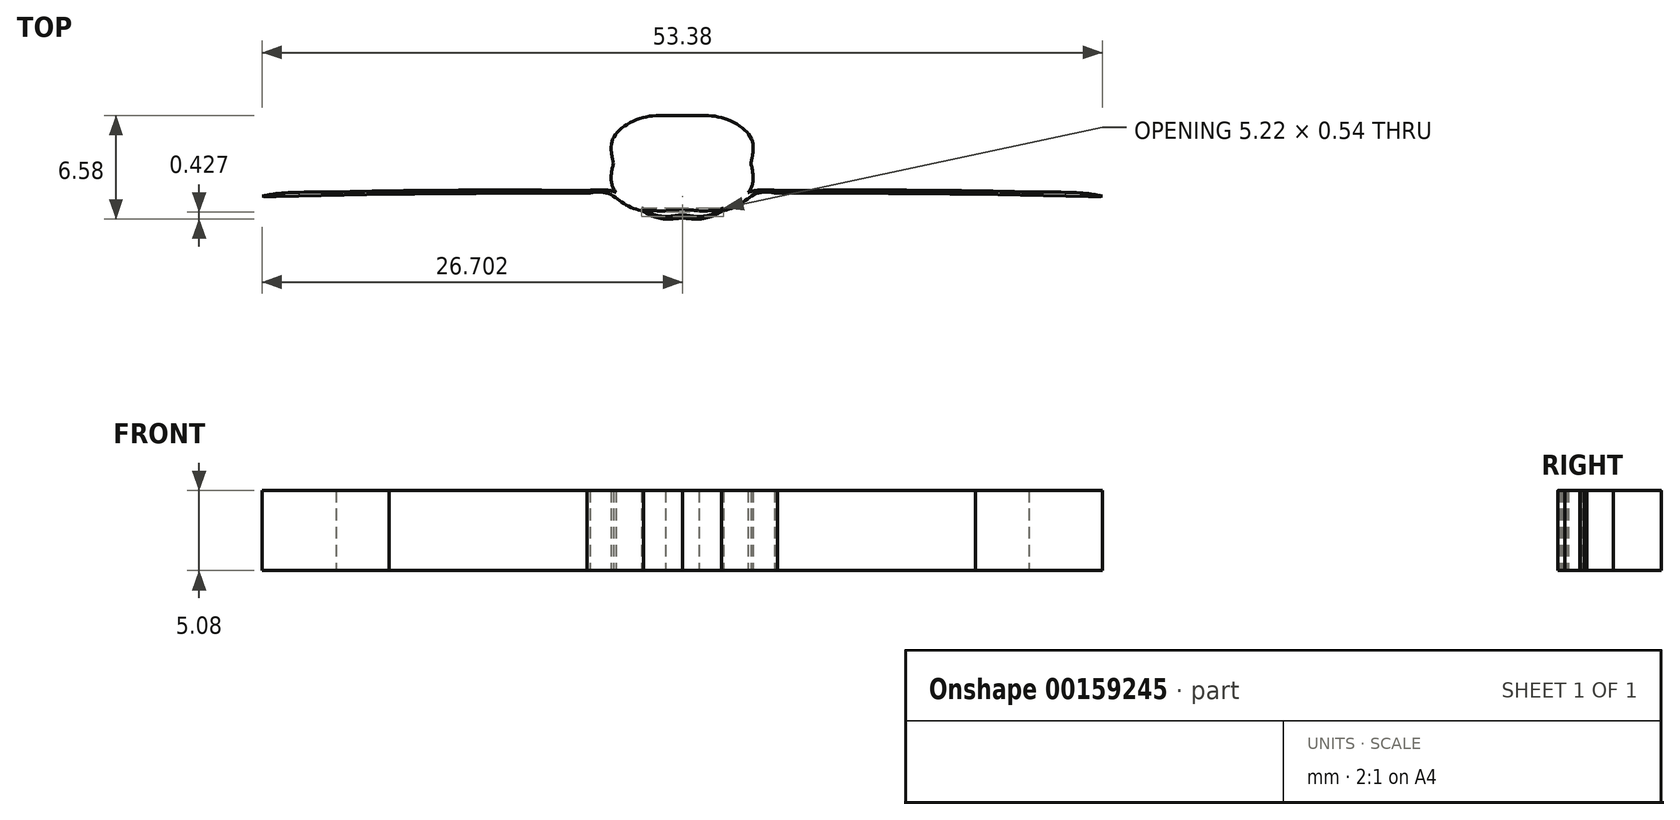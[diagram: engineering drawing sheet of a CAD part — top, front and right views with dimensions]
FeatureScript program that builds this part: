
annotation { "Feature Type Name" : "Feature", "Feature Type Description" : "" }
export const myFeature = defineFeature(function(context is Context, id is Id, definition is map)
    precondition{}
    {
        {
            var Q0;
            Q0=qCreatedBy(makeId("Top.planeOp"),FACE);
            var sketch = newSketch(context, id + "F0", { "sketchPlane" : qUnion([Q0])});
            skFitSpline(sketch, "E0.0", {"points": [v(2.56, 4.31) * mm, v(1.8, 4.62) * mm, v(0.78, 4.68) * mm, v(0.36, 4.7) * mm]});
            skFitSpline(sketch, "E0.1", {"points": [v(0.36, 4.7) * mm, v(0.23, 4.7) * mm, v(0.16, 4.7) * mm]});
            skFitSpline(sketch, "E0.2", {"points": [v(0.16, 4.7) * mm, v(-0.26, 4.68) * mm, v(-1.28, 4.62) * mm, v(-2.04, 4.31) * mm]});
            skFitSpline(sketch, "E0.3", {"points": [v(-2.04, 4.31) * mm, v(-3.03, 3.9) * mm, v(-4.04, 3.12) * mm, v(-4.9, 2.4) * mm]});
            skFitSpline(sketch, "E0.4", {"points": [v(-4.9, 2.4) * mm, v(-5.77, 1.67) * mm, v(-7.19, 1.69) * mm]});
            skLineSegment(sketch, "E0.5", {"start": v(-7.19, 1.69) * mm, "end": v(-11.13, 1.5) * mm});
            skFitSpline(sketch, "E0.6", {"points": [v(-11.13, 1.5) * mm, v(-13.37, 1.43) * mm, v(-14.49, 1.25) * mm]});
            skFitSpline(sketch, "E0.7", {"points": [v(-14.49, 1.25) * mm, v(-15.6, 1.08) * mm, v(-16.05, 0.62) * mm]});
            skFitSpline(sketch, "E0.8", {"points": [v(-16.05, 0.57) * mm, v(-15.47, 0.83) * mm, v(-13.7, 0.8) * mm]});
            skFitSpline(sketch, "E0.9", {"points": [v(-13.7, 0.8) * mm, v(-6.27, 1.03) * mm, v(-5.52, 1.06) * mm]});
            skFitSpline(sketch, "E0.10", {"points": [v(-5.52, 1.06) * mm, v(-4.76, 1.1) * mm, v(-4.2, 1.73) * mm, v(-3.94, 2.07) * mm]});
            skFitSpline(sketch, "E0.11", {"points": [v(-3.94, 2.07) * mm, v(-3.67, 2.4) * mm, v(-2.98, 3) * mm, v(-2.1, 3.4) * mm]});
            skFitSpline(sketch, "E0.12", {"points": [v(-2.1, 3.4) * mm, v(-1.39, 3.73) * mm, v(-0.18, 3.8) * mm, v(0.27, 3.81) * mm]});
            skFitSpline(sketch, "E0.13", {"points": [v(0.27, 3.81) * mm, v(0.71, 3.8) * mm, v(1.92, 3.73) * mm, v(2.63, 3.4) * mm]});
            skFitSpline(sketch, "E0.14", {"points": [v(2.63, 3.4) * mm, v(3.51, 2.99) * mm, v(4.2, 2.4) * mm, v(4.46, 2.05) * mm]});
            skFitSpline(sketch, "E0.15", {"points": [v(4.46, 2.05) * mm, v(4.73, 1.71) * mm, v(5.29, 1.08) * mm, v(6.04, 1.05) * mm]});
            skFitSpline(sketch, "E0.16", {"points": [v(6.04, 1.05) * mm, v(6.8, 1.01) * mm, v(14.23, 0.78) * mm]});
            skFitSpline(sketch, "E0.17", {"points": [v(14.23, 0.78) * mm, v(16, 0.83) * mm, v(16.58, 0.56) * mm]});
            skFitSpline(sketch, "E0.18", {"points": [v(16.57, 0.62) * mm, v(16.12, 1.08) * mm, v(15, 1.25) * mm]});
            skFitSpline(sketch, "E0.19", {"points": [v(15, 1.25) * mm, v(13.9, 1.43) * mm, v(11.65, 1.5) * mm]});
            skLineSegment(sketch, "E0.20", {"start": v(11.65, 1.5) * mm, "end": v(7.7, 1.69) * mm});
            skFitSpline(sketch, "E0.21", {"points": [v(7.7, 1.69) * mm, v(6.28, 1.67) * mm, v(5.42, 2.4) * mm]});
            skFitSpline(sketch, "E0.22", {"points": [v(5.42, 2.4) * mm, v(4.56, 3.12) * mm, v(3.55, 3.9) * mm, v(2.56, 4.31) * mm]});
            skFitSpline(sketch, "E0.23", {"points": [v(11.54, 0.53) * mm, v(10.6, 0.53) * mm, v(6.1, 0.62) * mm, v(5.87, 0.6) * mm]});
            skFitSpline(sketch, "E0.24", {"points": [v(5.87, 0.6) * mm, v(5.63, 0.6) * mm, v(5.53, 0.54) * mm]});
            skFitSpline(sketch, "E0.25", {"points": [v(5.53, 0.54) * mm, v(5.4, 0.45) * mm, v(5.26, 0.35) * mm]});
            skFitSpline(sketch, "E0.26", {"points": [v(5.26, 0.35) * mm, v(5.11, 0.24) * mm, v(5.32, 0.2) * mm]});
            skLineSegment(sketch, "E0.27", {"start": v(5.32, 0.2) * mm, "end": v(7.9, 0.18) * mm});
            skFitSpline(sketch, "E0.28", {"points": [v(7.9, 0.18) * mm, v(9.26, 0.17) * mm, v(12.3, 0.15) * mm, v(12.82, 0.13) * mm]});
            skFitSpline(sketch, "E0.29", {"points": [v(15.92, 0.47) * mm, v(15.36, 0.45) * mm, v(12.48, 0.53) * mm, v(11.54, 0.53) * mm]});
            skFitSpline(sketch, "E0.30", {"points": [v(12.82, 0.13) * mm, v(13.34, 0.11) * mm, v(17.15, 0.06) * mm]});
            skFitSpline(sketch, "E0.31", {"points": [v(17.15, 0.06) * mm, v(20.7, -0.03) * mm, v(21.42, -0.07) * mm]});
            skFitSpline(sketch, "E0.32", {"points": [v(21.42, -0.07) * mm, v(21.97, -0.1) * mm, v(22.26, -0.3) * mm, v(22.37, -0.4) * mm]});
            skFitSpline(sketch, "E0.33", {"points": [v(22.4, -0.34) * mm, v(22.35, -0.29) * mm, v(21.8, 0.22) * mm, v(20.33, 0.42) * mm]});
            skFitSpline(sketch, "E0.34", {"points": [v(20.33, 0.42) * mm, v(19.17, 0.58) * mm, v(17.67, 0.6) * mm, v(16.96, 0.61) * mm]});
            skFitSpline(sketch, "E0.35", {"points": [v(16.96, 0.61) * mm, v(16.72, 0.62) * mm, v(16.57, 0.62) * mm]});
            skFitSpline(sketch, "E0.36", {"points": [v(16.57, 0.57) * mm, v(16.5, 0.5) * mm, v(16.3, 0.5) * mm, v(15.92, 0.47) * mm]});
            skFitSpline(sketch, "E0.37", {"points": [v(22.83, -0.36) * mm, v(22.62, -0.35) * mm, v(22.4, -0.34) * mm]});
            skFitSpline(sketch, "E0.38", {"points": [v(25.42, -0.59) * mm, v(24.54, -0.47) * mm, v(23.45, -0.4) * mm, v(22.83, -0.36) * mm]});
            skFitSpline(sketch, "E0.39", {"points": [v(27.22, -1.18) * mm, v(26.73, -0.77) * mm, v(25.42, -0.59) * mm]});
            skFitSpline(sketch, "E0.40", {"points": [v(22.37, -0.4) * mm, v(22.35, -0.43) * mm, v(22.3, -0.46) * mm, v(22.18, -0.47) * mm]});
            skFitSpline(sketch, "E0.41", {"points": [v(22.18, -0.47) * mm, v(21.91, -0.5) * mm, v(20.73, -0.5) * mm, v(18.04, -0.47) * mm]});
            skFitSpline(sketch, "E0.42", {"points": [v(18.04, -0.47) * mm, v(15.35, -0.44) * mm, v(11.53, -0.4) * mm]});
            skLineSegment(sketch, "E0.43", {"start": v(11.53, -0.4) * mm, "end": v(7.76, -0.36) * mm});
            skLineSegment(sketch, "E1.0", {"start": v(7.76, -0.36) * mm, "end": v(5.7, -0.33) * mm});
            skFitSpline(sketch, "E1.1", {"points": [v(5.7, -0.33) * mm, v(5.47, -0.3) * mm, v(5.24, -0.44) * mm]});
            skFitSpline(sketch, "E1.2", {"points": [v(5.24, -0.44) * mm, v(5.02, -0.59) * mm, v(5.03, -0.6) * mm]});
            skFitSpline(sketch, "E1.3", {"points": [v(5.03, -0.6) * mm, v(4.93, -0.7) * mm, v(5.12, -0.7) * mm]});
            skFitSpline(sketch, "E1.4", {"points": [v(5.12, -0.7) * mm, v(5.31, -0.7) * mm, v(8.17, -0.7) * mm]});
            skLineSegment(sketch, "E1.5", {"start": v(8.17, -0.7) * mm, "end": v(11.57, -0.68) * mm});
            skLineSegment(sketch, "E1.6", {"start": v(11.57, -0.68) * mm, "end": v(15.14, -0.7) * mm});
            skLineSegment(sketch, "E1.7", {"start": v(15.14, -0.7) * mm, "end": v(18.12, -0.75) * mm});
            skLineSegment(sketch, "E1.8", {"start": v(18.12, -0.75) * mm, "end": v(22.16, -0.82) * mm});
            skFitSpline(sketch, "E1.9", {"points": [v(22.16, -0.82) * mm, v(25.58, -0.94) * mm, v(25.8, -0.95) * mm]});
            skFitSpline(sketch, "E1.10", {"points": [v(25.8, -0.95) * mm, v(26, -0.96) * mm, v(26.68, -1) * mm, v(27.22, -1.21) * mm]});
            skFitSpline(sketch, "E1.11", {"points": [v(27.22, -1.18) * mm, v(26.73, -0.77) * mm, v(25.42, -0.59) * mm]});
            skFitSpline(sketch, "E1.12", {"points": [v(25.42, -0.59) * mm, v(24.54, -0.47) * mm, v(23.45, -0.4) * mm, v(22.83, -0.36) * mm]});
            skFitSpline(sketch, "E2.0", {"points": [v(26.95, -1.32) * mm, v(26.59, -1.25) * mm, v(25.5, -1.12) * mm, v(22.26, -1.06) * mm]});
            skFitSpline(sketch, "E2.1", {"points": [v(22.26, -1.06) * mm, v(17.48, -0.97) * mm, v(9.2, -0.93) * mm]});
            skLineSegment(sketch, "E2.2", {"start": v(9.2, -0.93) * mm, "end": v(6.13, -0.95) * mm});
            skFitSpline(sketch, "E2.3", {"points": [v(6.13, -0.95) * mm, v(4.7, -1) * mm, v(4.08, -1.35) * mm]});
            skFitSpline(sketch, "E2.4", {"points": [v(4.08, -1.35) * mm, v(3.49, -1.68) * mm, v(1.93, -2.53) * mm, v(0.27, -2.48) * mm]});
            skFitSpline(sketch, "E2.5", {"points": [v(2.73, -2.3) * mm, v(3.92, -1.83) * mm, v(4.98, -1.15) * mm, v(6.3, -1.13) * mm]});
            skFitSpline(sketch, "E2.6", {"points": [v(6.3, -1.13) * mm, v(7.64, -1.11) * mm, v(18.88, -1.18) * mm]});
            skLineSegment(sketch, "E2.7", {"start": v(18.88, -1.18) * mm, "end": v(26.05, -1.35) * mm});
            skFitSpline(sketch, "E2.8", {"points": [v(26.05, -1.35) * mm, v(26.59, -1.35) * mm, v(26.95, -1.32) * mm]});
            skFitSpline(sketch, "E2.9", {"points": [v(0.26, -2.71) * mm, v(0.36, -2.71) * mm, v(1.6, -2.75) * mm, v(2.73, -2.3) * mm]});
            skFitSpline(sketch, "E2.10", {"points": [v(-2.21, -2.3) * mm, v(-1.07, -2.75) * mm, v(0.16, -2.71) * mm, v(0.26, -2.71) * mm]});
            skFitSpline(sketch, "E2.11", {"points": [v(0.27, -2.48) * mm, v(-1.41, -2.53) * mm, v(-2.97, -1.68) * mm, v(-3.56, -1.35) * mm]});
            skFitSpline(sketch, "E2.12", {"points": [v(-5.79, -1.13) * mm, v(-4.46, -1.15) * mm, v(-3.4, -1.83) * mm, v(-2.21, -2.3) * mm]});
            skFitSpline(sketch, "E2.13", {"points": [v(-18.36, -1.18) * mm, v(-7.12, -1.11) * mm, v(-5.79, -1.13) * mm]});
            skLineSegment(sketch, "E2.14", {"start": v(-5.6, -0.95) * mm, "end": v(-8.68, -0.93) * mm});
            skFitSpline(sketch, "E2.15", {"points": [v(-3.56, -1.35) * mm, v(-4.17, -1) * mm, v(-5.6, -0.95) * mm]});
            skFitSpline(sketch, "E2.16", {"points": [v(-8.68, -0.93) * mm, v(-16.96, -0.97) * mm, v(-21.74, -1.06) * mm]});
            skLineSegment(sketch, "E2.17", {"start": v(-25.53, -1.35) * mm, "end": v(-18.36, -1.18) * mm});
            skFitSpline(sketch, "E2.18", {"points": [v(-21.74, -1.06) * mm, v(-24.99, -1.12) * mm, v(-26.07, -1.25) * mm, v(-26.43, -1.32) * mm]});
            skFitSpline(sketch, "E2.19", {"points": [v(-26.43, -1.32) * mm, v(-26.07, -1.35) * mm, v(-25.53, -1.35) * mm]});
            skFitSpline(sketch, "E3.0", {"points": [v(-5.35, 0.6) * mm, v(-5.58, 0.62) * mm, v(-10.09, 0.53) * mm, v(-11.02, 0.53) * mm]});
            skFitSpline(sketch, "E3.1", {"points": [v(-5.01, 0.54) * mm, v(-5.11, 0.6) * mm, v(-5.35, 0.6) * mm]});
            skFitSpline(sketch, "E3.2", {"points": [v(-4.74, 0.35) * mm, v(-4.88, 0.45) * mm, v(-5.01, 0.54) * mm]});
            skFitSpline(sketch, "E3.3", {"points": [v(-4.8, 0.2) * mm, v(-4.6, 0.24) * mm, v(-4.74, 0.35) * mm]});
            skLineSegment(sketch, "E3.4", {"start": v(-7.39, 0.18) * mm, "end": v(-4.8, 0.2) * mm});
            skFitSpline(sketch, "E3.5", {"points": [v(-12.3, 0.13) * mm, v(-11.78, 0.15) * mm, v(-8.74, 0.17) * mm, v(-7.39, 0.18) * mm]});
            skFitSpline(sketch, "E3.6", {"points": [v(-11.02, 0.53) * mm, v(-11.96, 0.53) * mm, v(-14.84, 0.45) * mm, v(-15.4, 0.47) * mm]});
            skFitSpline(sketch, "E3.7", {"points": [v(-16.63, 0.06) * mm, v(-12.82, 0.11) * mm, v(-12.3, 0.13) * mm]});
            skFitSpline(sketch, "E3.8", {"points": [v(-15.4, 0.47) * mm, v(-15.79, 0.5) * mm, v(-15.97, 0.5) * mm, v(-16.05, 0.57) * mm]});
            skFitSpline(sketch, "E3.9", {"points": [v(-20.9, -0.07) * mm, v(-20.18, -0.03) * mm, v(-16.63, 0.06) * mm]});
            skFitSpline(sketch, "E3.10", {"points": [v(-21.85, -0.4) * mm, v(-21.74, -0.3) * mm, v(-21.46, -0.1) * mm, v(-20.9, -0.07) * mm]});
            skFitSpline(sketch, "E3.11", {"points": [v(-19.8, 0.42) * mm, v(-21.29, 0.22) * mm, v(-21.83, -0.29) * mm, v(-21.88, -0.34) * mm]});
            skFitSpline(sketch, "E3.12", {"points": [v(-16.45, 0.61) * mm, v(-17.15, 0.6) * mm, v(-18.65, 0.58) * mm, v(-19.8, 0.42) * mm]});
            skFitSpline(sketch, "E3.13", {"points": [v(-21.88, -0.34) * mm, v(-22.1, -0.35) * mm, v(-22.31, -0.36) * mm]});
            skFitSpline(sketch, "E3.14", {"points": [v(-22.31, -0.36) * mm, v(-22.93, -0.4) * mm, v(-24.02, -0.47) * mm, v(-24.9, -0.59) * mm]});
            skFitSpline(sketch, "E3.15", {"points": [v(-24.9, -0.59) * mm, v(-26.21, -0.77) * mm, v(-26.7, -1.18) * mm]});
            skFitSpline(sketch, "E3.16", {"points": [v(-26.7, -1.21) * mm, v(-26.16, -1) * mm, v(-25.49, -0.96) * mm, v(-25.27, -0.95) * mm]});
            skFitSpline(sketch, "E3.17", {"points": [v(-25.27, -0.95) * mm, v(-25.06, -0.94) * mm, v(-21.64, -0.82) * mm]});
            skLineSegment(sketch, "E3.18", {"start": v(-21.64, -0.82) * mm, "end": v(-17.6, -0.75) * mm});
            skFitSpline(sketch, "E3.19", {"points": [v(-17.52, -0.47) * mm, v(-20.21, -0.5) * mm, v(-21.4, -0.5) * mm, v(-21.66, -0.47) * mm]});
            skFitSpline(sketch, "E3.20", {"points": [v(-21.66, -0.47) * mm, v(-21.78, -0.46) * mm, v(-21.83, -0.43) * mm, v(-21.85, -0.4) * mm]});
            skLineSegment(sketch, "E3.21", {"start": v(-17.6, -0.75) * mm, "end": v(-14.62, -0.7) * mm});
            skFitSpline(sketch, "E3.22", {"points": [v(-11, -0.4) * mm, v(-14.83, -0.44) * mm, v(-17.52, -0.47) * mm]});
            skLineSegment(sketch, "E3.23", {"start": v(-14.62, -0.7) * mm, "end": v(-11.05, -0.68) * mm});
            skLineSegment(sketch, "E3.24", {"start": v(-11.05, -0.68) * mm, "end": v(-7.65, -0.7) * mm});
            skLineSegment(sketch, "E3.25", {"start": v(-7.24, -0.36) * mm, "end": v(-11, -0.4) * mm});
            skLineSegment(sketch, "E3.26", {"start": v(-5.19, -0.33) * mm, "end": v(-7.24, -0.36) * mm});
            skFitSpline(sketch, "E3.27", {"points": [v(-4.72, -0.44) * mm, v(-4.95, -0.3) * mm, v(-5.19, -0.33) * mm]});
            skFitSpline(sketch, "E3.28", {"points": [v(-4.5, -0.6) * mm, v(-4.5, -0.59) * mm, v(-4.72, -0.44) * mm]});
            skFitSpline(sketch, "E3.29", {"points": [v(-4.6, -0.7) * mm, v(-4.41, -0.7) * mm, v(-4.5, -0.6) * mm]});
            skFitSpline(sketch, "E3.30", {"points": [v(-7.65, -0.7) * mm, v(-4.8, -0.7) * mm, v(-4.6, -0.7) * mm]});
            skFitSpline(sketch, "E4.0", {"points": [v(0.25, -2.14) * mm, v(2.66, -2.14) * mm, v(4.61, -0.83) * mm, v(4.61, 0.77) * mm]});
            skFitSpline(sketch, "E4.1", {"points": [v(-4.12, 0.77) * mm, v(-4.12, -0.83) * mm, v(-2.16, -2.14) * mm, v(0.25, -2.14) * mm]});
            skFitSpline(sketch, "E4.2", {"points": [v(0.25, 3.69) * mm, v(-2.16, 3.69) * mm, v(-4.12, 2.38) * mm, v(-4.12, 0.77) * mm]});
            skFitSpline(sketch, "E4.3", {"points": [v(4.61, 0.77) * mm, v(4.61, 2.38) * mm, v(2.66, 3.69) * mm, v(0.25, 3.69) * mm]});
            skArc(sketch, "E5", {"start": v(27.22, -1.21) * mm, "mid": v(27.23, -1.2) * mm, "end": v(27.22, -1.18) * mm});
            skLineSegment(sketch, "E6", {"start": v(-16.05, 0.57) * mm, "end": v(-16.05, 0.62) * mm});
            skLineSegment(sketch, "E7", {"start": v(-16.45, 0.61) * mm, "end": v(-16.05, 0.62) * mm});
            skLineSegment(sketch, "E8", {"start": v(-26.7, -1.18) * mm, "end": v(-26.7, -1.21) * mm});
            skSolve(sketch);
        }
        {
            var Q0;
            Q0 = qSketchRegion(id + "F0", true);
            extrude(context, id + "F1", {"entities" : qUnion([Q0]), "depth" : 5.08 * mm});
        }
    });
